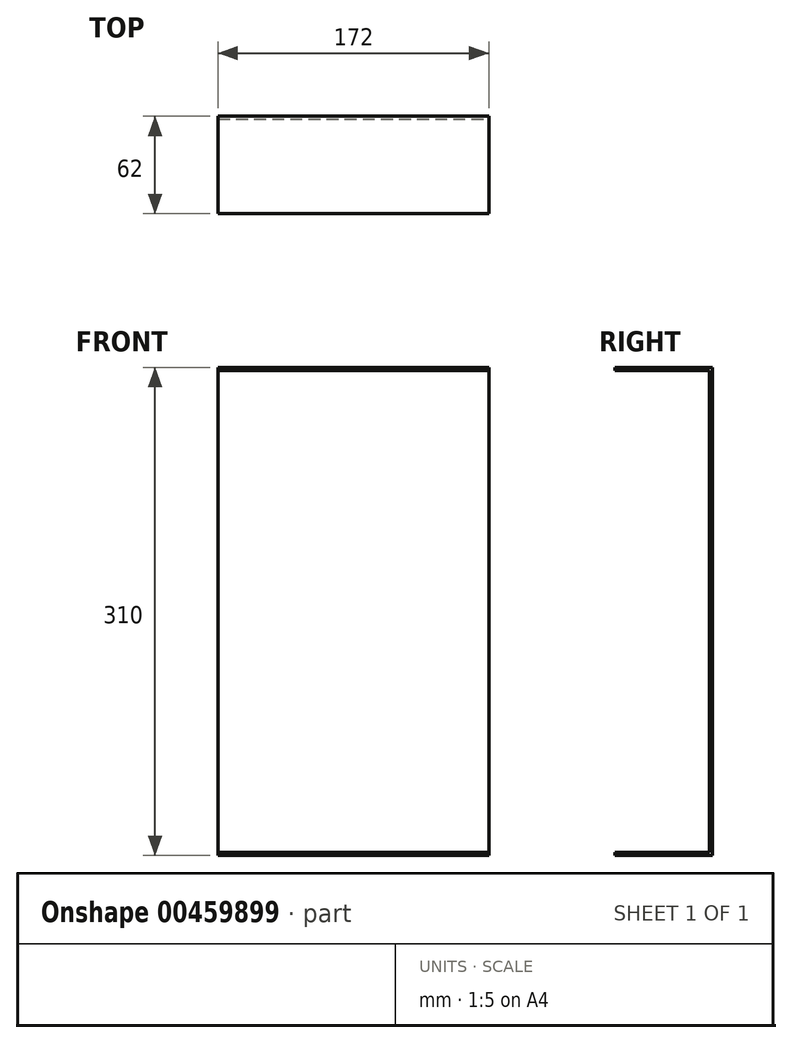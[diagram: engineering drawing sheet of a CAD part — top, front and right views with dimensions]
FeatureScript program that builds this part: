
annotation { "Feature Type Name" : "Feature", "Feature Type Description" : "" }
export const myFeature = defineFeature(function(context is Context, id is Id, definition is map)
    precondition{}
    {
        {
            var Q0;
            Q0=qCreatedBy(makeId("Front.planeOp"),FACE);
            var sketch = newSketch(context, id + "F0", { "sketchPlane" : qUnion([Q0])});
            skLineSegment(sketch, "E0.bottom", {"start": v(86, -155) * mm, "end": v(-86, -155) * mm});
            skLineSegment(sketch, "E0.top", {"start": v(86, 155) * mm, "end": v(-86, 155) * mm});
            skLineSegment(sketch, "E0.left", {"start": v(86, -155) * mm, "end": v(86, 155) * mm});
            skLineSegment(sketch, "E0.right", {"start": v(-86, -155) * mm, "end": v(-86, 155) * mm});
            skPoint(sketch, "E0.middle", {"position": v(0, 0) * mm});
            skLineSegment(sketch, "E1", {"start": v(-86, 153) * mm, "end": v(86, 153) * mm});
            skLineSegment(sketch, "E2", {"start": v(-86, -153) * mm, "end": v(86, -153) * mm});
            skSolve(sketch);
        }
        {
            var Q0;
            {var subQ0=sQuery(id+"F0.wireOp",EDGE,"E1");Q0=makeQuery(id+"F0.imprint","IMPRINT",FACE,{"disambiguationData":[TD([[makeQuery(id+"F0.imprint","IMPRINT",EDGE,{"derivedFrom":subQ0}),-1.0]])]});}
            extrude(context, id + "F1", {"entities" : qUnion([Q0]), "depth" : 2 * mm});
        }
        {
            var Q0;
            {var subQ0=sQuery(id+"F0.wireOp",EDGE,"E0.top");Q0=makeQuery(id+"F0.imprint","IMPRINT",FACE,{"disambiguationData":[TD([[makeQuery(id+"F0.imprint","IMPRINT",EDGE,{"derivedFrom":subQ0}),1.0]])]});}
            extrude(context, id + "F2", {"entities" : qUnion([Q0]), "operationType" : NewBodyOperationType.ADD, "depth" : 62 * mm});
        }
        {
            var Q0;
            {var subQ0=sQuery(id+"F0.wireOp",EDGE,"E0.bottom");Q0=makeQuery(id+"F0.imprint","IMPRINT",FACE,{"disambiguationData":[TD([[makeQuery(id+"F0.imprint","IMPRINT",EDGE,{"derivedFrom":subQ0}),-1.0]])]});}
            extrude(context, id + "F3", {"entities" : qUnion([Q0]), "operationType" : NewBodyOperationType.ADD, "depth" : 62 * mm});
        }
    });
